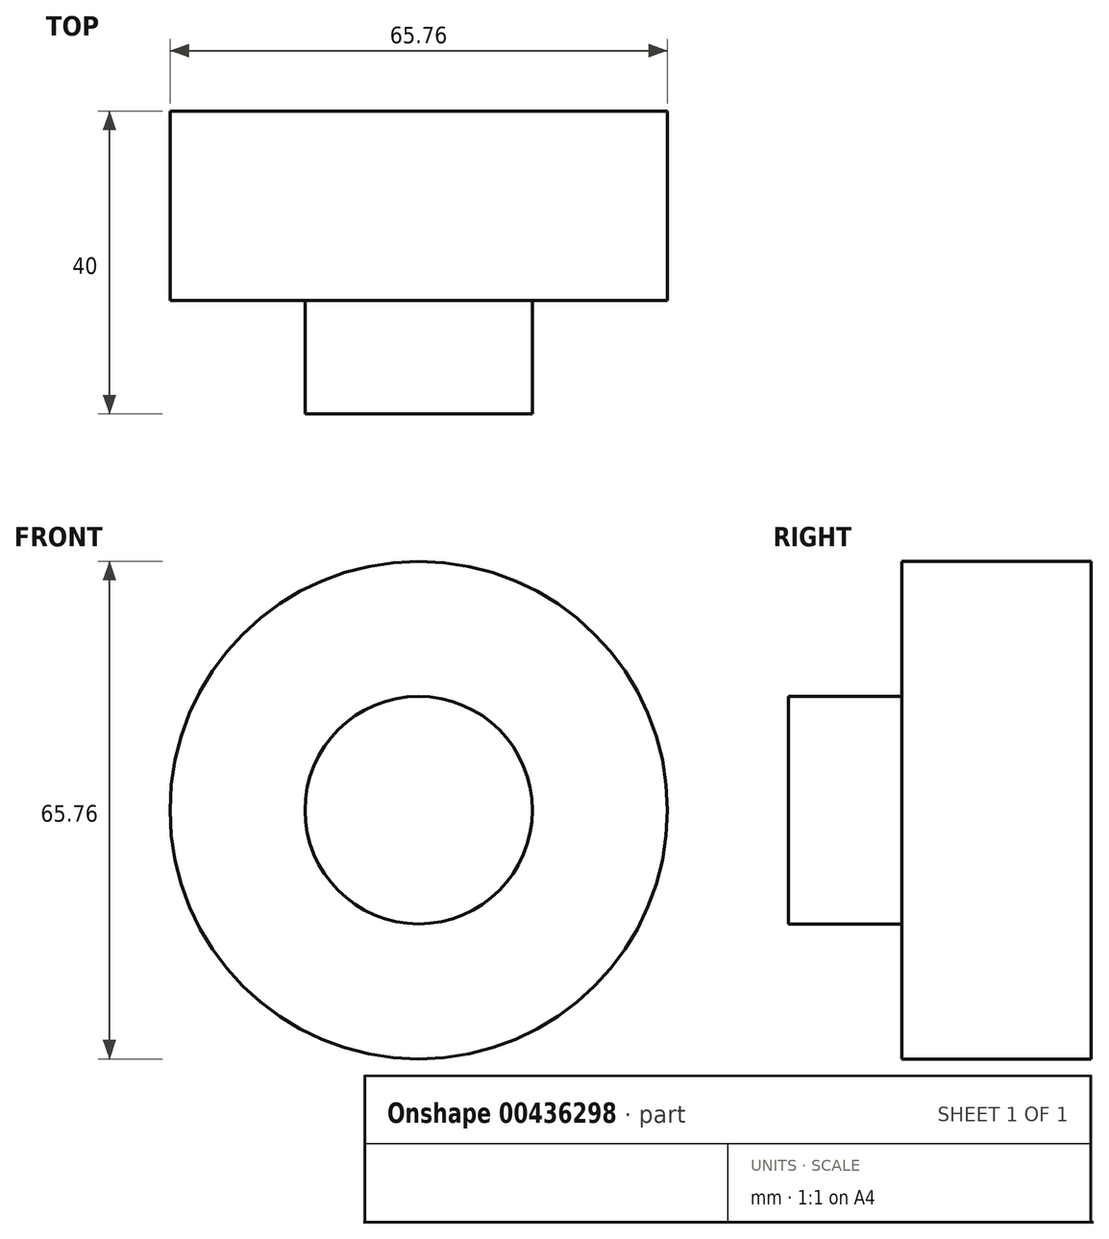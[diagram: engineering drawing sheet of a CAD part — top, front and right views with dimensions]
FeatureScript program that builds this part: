
annotation { "Feature Type Name" : "Feature", "Feature Type Description" : "" }
export const myFeature = defineFeature(function(context is Context, id is Id, definition is map)
    precondition{}
    {
        {
            var Q0;
            Q0=qCreatedBy(makeId("Front.planeOp"),FACE);
            var sketch = newSketch(context, id + "F0", { "sketchPlane" : qUnion([Q0])});
            skCircle(sketch, "E0", {"center": v(0, 0) * mm, "radius": 32.88 * mm});
            skSolve(sketch);
        }
        {
            var Q0;
            Q0=qCreatedBy(makeId("Front.planeOp"),FACE);
            var sketch = newSketch(context, id + "F1", { "sketchPlane" : qUnion([Q0])});
            skCircle(sketch, "E1", {"center": v(0, 0) * mm, "radius": 23.13 * mm});
            skSolve(sketch);
        }
        {
            var Q0;
            Q0=makeQuery(id+"F0.imprint","IMPRINT",FACE,{"disambiguationData":[TD([[makeQuery(id+"F0.imprint","IMPRINT",EDGE,{"derivedFrom":sQuery(id+"F0.wireOp",EDGE,"E0")}),1.0]])]});
            extrude(context, id + "F2", {"entities" : qUnion([Q0]), "depth" : 25 * mm});
        }
        {
            var Q0;
            Q0=makeQuery(id+"F1.imprint","IMPRINT",FACE,{"disambiguationData":[TD([[makeQuery(id+"F1.imprint","IMPRINT",EDGE,{"derivedFrom":sQuery(id+"F1.wireOp",EDGE,"E1")}),1.0]])]});
            extrude(context, id + "F3", {"entities" : qUnion([Q0]), "operationType" : NewBodyOperationType.ADD, "depth" : 15 * mm});
        }
        {
            var Q0;
            Q0=makeQuery(id+"F2.opExtrude","CAP_FACE",FACE,{"disambiguationData":[OSD([sQuery(id+"F0.wireOp",EDGE,"E0")])],"isStart":false});
            var sketch = newSketch(context, id + "F4", { "sketchPlane" : qUnion([Q0])});
            skCircle(sketch, "E2", {"center": v(0, 0) * mm, "radius": 15.03 * mm});
            skSolve(sketch);
        }
        {
            var Q0;
            Q0 = qSketchRegion(id + "F4", true);
            extrude(context, id + "F5", {"entities" : qUnion([Q0]), "operationType" : NewBodyOperationType.ADD, "depth" : 15 * mm});
        }
    });
